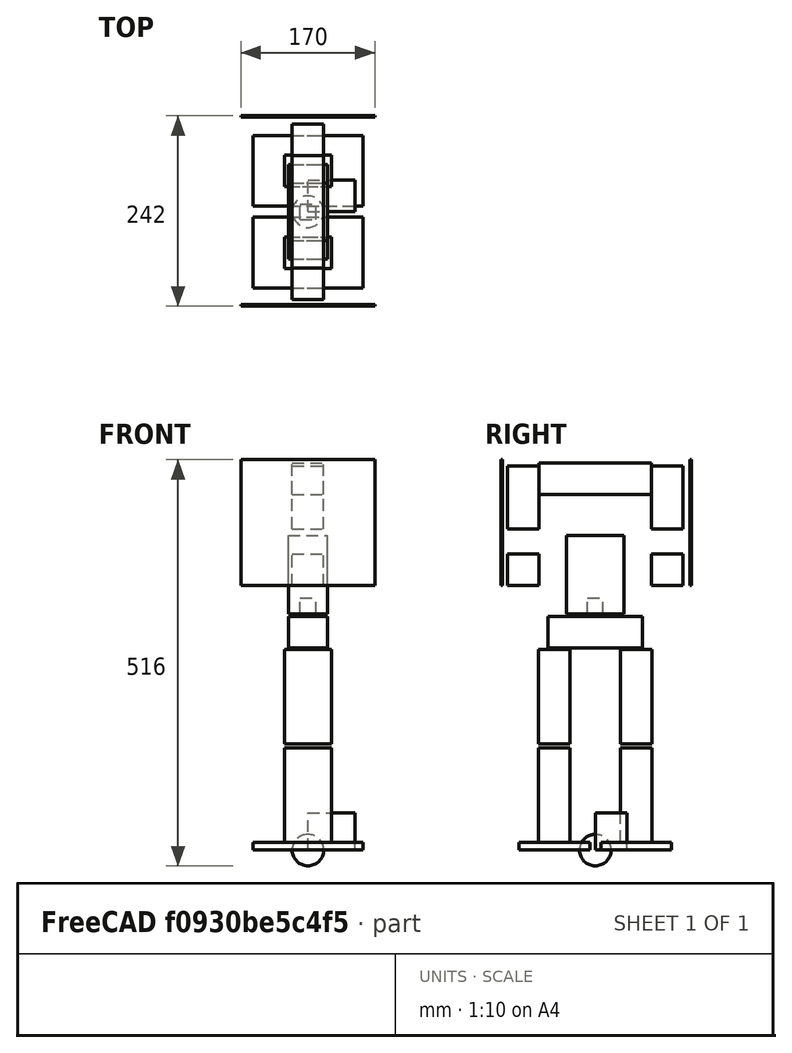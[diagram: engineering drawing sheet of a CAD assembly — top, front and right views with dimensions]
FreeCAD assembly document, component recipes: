
FREECAD ASSEMBLY — COMPONENT RECIPES ("mj_urdf")

This assembly document has 21 components, labeled P0..P20 below (a component is one placed body or linked part). 0 of them carry a construction recipe — the FreeCAD feature program that regenerates the part from scratch, quoted from this document or its linked companion documents; the rest are supplied as boundary geometry only. No exploded tour is included for this assembly.
COMPONENT P0 — geometry summary ("left_sholder001"; no construction recipe available for this part):
  bounding box: 80.0 x 40.0 x 40.0 mm
  tessellated surface: 12 triangles
  volume: 128000 mm^3 (100% of its bounding box)
  symmetry: 2-fold rotationally symmetric about the x axis; 2-fold rotationally symmetric about the y axis; 4-fold rotationally symmetric about the z axis; mirror-symmetric across its x mid-plane, z mid-plane
COMPONENT P1 — geometry summary ("real_l_body001_"; no construction recipe available for this part):
  bounding box: 161.0 x 143.0 x 50.0 mm
  tessellated surface: 36 triangles
  volume: 601800 mm^3 (52% of its bounding box)
COMPONENT P2 — geometry summary ("real_l_left_ankle001_"; no construction recipe available for this part):
  bounding box: 40.0 x 40.0 x 40.0 mm
  tessellated surface: 8,000 triangles
  volume: 33510 mm^3 (52% of its bounding box)
  symmetry: revolution-symmetric about the x axis through its bounding-box center; revolution-symmetric about the y axis through its bounding-box center; revolution-symmetric about the z axis through its bounding-box center; mirror-symmetric across its x mid-plane, y mid-plane, z mid-plane
COMPONENT P3 — geometry summary ("real_l_left_arm001_"; no construction recipe available for this part):
  bounding box: 80.0 x 40.0 x 40.0 mm
  tessellated surface: 12 triangles
  volume: 128000 mm^3 (100% of its bounding box)
  symmetry: 2-fold rotationally symmetric about the x axis; 2-fold rotationally symmetric about the y axis; 4-fold rotationally symmetric about the z axis; mirror-symmetric across its x mid-plane, z mid-plane
COMPONENT P4 — geometry summary ("real_l_left_hand001_"; no construction recipe available for this part):
  bounding box: 170.0 x 160.0 x 2.0 mm
  tessellated surface: 12 triangles
  volume: 54400 mm^3 (100% of its bounding box)
  symmetry: 2-fold rotationally symmetric about the x axis; 2-fold rotationally symmetric about the y axis; 2-fold rotationally symmetric about the z axis; mirror-symmetric across its x mid-plane, y mid-plane, z mid-plane
COMPONENT P5 — geometry summary ("real_l_left_hip001_"; no construction recipe available for this part):
  bounding box: 40.0 x 40.0 x 40.0 mm
  tessellated surface: 8,000 triangles
  volume: 33510 mm^3 (52% of its bounding box)
  symmetry: revolution-symmetric about the x axis through its bounding-box center; revolution-symmetric about the y axis through its bounding-box center; revolution-symmetric about the z axis through its bounding-box center; mirror-symmetric across its x mid-plane, y mid-plane, z mid-plane
COMPONENT P6 — geometry summary ("real_l_left_knee001_"; no construction recipe available for this part):
  bounding box: 60.0 x 47.0 x 40.0 mm
  tessellated surface: 12 triangles
  volume: 112800 mm^3 (100% of its bounding box)
  symmetry: 2-fold rotationally symmetric about the z axis; mirror-symmetric across its y mid-plane
COMPONENT P7 — geometry summary ("real_l_left_shin001_"; no construction recipe available for this part):
  bounding box: 120.0 x 60.0 x 40.0 mm
  tessellated surface: 12 triangles
  volume: 288000 mm^3 (100% of its bounding box)
  symmetry: 2-fold rotationally symmetric about the x axis; 2-fold rotationally symmetric about the y axis; mirror-symmetric across its y mid-plane
COMPONENT P8 — geometry summary ("real_l_left_sole001_"; no construction recipe available for this part):
  bounding box: 140.0 x 90.0 x 10.0 mm
  tessellated surface: 12 triangles
  volume: 126000 mm^3 (100% of its bounding box)
  symmetry: 2-fold rotationally symmetric about the y axis; 2-fold rotationally symmetric about the z axis; mirror-symmetric across its x mid-plane, y mid-plane, z mid-plane
COMPONENT P9 — geometry summary ("real_l_left_thigh001_"; no construction recipe available for this part):
  bounding box: 120.0 x 60.0 x 40.0 mm
  tessellated surface: 12 triangles
  volume: 288000 mm^3 (100% of its bounding box)
  symmetry: 2-fold rotationally symmetric about the x axis; 2-fold rotationally symmetric about the y axis; mirror-symmetric across its y mid-plane
COMPONENT P10 — geometry summary ("real_l_left_wrist001_"; no construction recipe available for this part):
  bounding box: 40.0 x 40.0 x 40.0 mm
  tessellated surface: 12 triangles
  volume: 64000 mm^3 (100% of its bounding box)
  symmetry: 4-fold rotationally symmetric about the x axis; 4-fold rotationally symmetric about the z axis; mirror-symmetric across its x mid-plane, y mid-plane, z mid-plane
COMPONENT P11 — geometry summary ("real_l_right_ankle001_"; no construction recipe available for this part):
  bounding box: 40.0 x 40.0 x 40.0 mm
  tessellated surface: 8,000 triangles
  volume: 33510 mm^3 (52% of its bounding box)
  symmetry: revolution-symmetric about the x axis through its bounding-box center; revolution-symmetric about the y axis through its bounding-box center; revolution-symmetric about the z axis through its bounding-box center; mirror-symmetric across its x mid-plane, y mid-plane, z mid-plane
COMPONENT P12 — geometry summary ("real_l_right_arm001_"; no construction recipe available for this part):
  bounding box: 80.0 x 40.0 x 40.0 mm
  tessellated surface: 12 triangles
  volume: 128000 mm^3 (100% of its bounding box)
  symmetry: 2-fold rotationally symmetric about the x axis; 2-fold rotationally symmetric about the y axis; 4-fold rotationally symmetric about the z axis; mirror-symmetric across its x mid-plane, z mid-plane
COMPONENT P13 — geometry summary ("real_l_right_hand001_"; no construction recipe available for this part):
  bounding box: 170.0 x 160.0 x 2.0 mm
  tessellated surface: 12 triangles
  volume: 54400 mm^3 (100% of its bounding box)
  symmetry: 2-fold rotationally symmetric about the x axis; 2-fold rotationally symmetric about the y axis; 2-fold rotationally symmetric about the z axis; mirror-symmetric across its x mid-plane, y mid-plane, z mid-plane
COMPONENT P14 — geometry summary ("real_l_right_hip001_"; no construction recipe available for this part):
  bounding box: 40.0 x 40.0 x 40.0 mm
  tessellated surface: 8,000 triangles
  volume: 33510 mm^3 (52% of its bounding box)
  symmetry: revolution-symmetric about the x axis through its bounding-box center; revolution-symmetric about the y axis through its bounding-box center; revolution-symmetric about the z axis through its bounding-box center; mirror-symmetric across its x mid-plane, y mid-plane, z mid-plane
COMPONENT P15 — geometry summary ("real_l_right_knee001_"; no construction recipe available for this part):
  bounding box: 60.0 x 47.0 x 40.0 mm
  tessellated surface: 12 triangles
  volume: 112800 mm^3 (100% of its bounding box)
  symmetry: 2-fold rotationally symmetric about the z axis; mirror-symmetric across its y mid-plane
COMPONENT P16 — geometry summary ("real_l_right_shin001_"; no construction recipe available for this part):
  bounding box: 120.0 x 60.0 x 40.0 mm
  tessellated surface: 12 triangles
  volume: 288000 mm^3 (100% of its bounding box)
  symmetry: 2-fold rotationally symmetric about the x axis; 2-fold rotationally symmetric about the y axis; 2-fold rotationally symmetric about the z axis; mirror-symmetric across its y mid-plane
COMPONENT P17 — geometry summary ("real_l_right_sole001_"; no construction recipe available for this part):
  bounding box: 140.0 x 90.0 x 10.0 mm
  tessellated surface: 12 triangles
  volume: 126000 mm^3 (100% of its bounding box)
  symmetry: 2-fold rotationally symmetric about the y axis; 2-fold rotationally symmetric about the z axis; mirror-symmetric across its x mid-plane, y mid-plane, z mid-plane
COMPONENT P18 — geometry summary ("real_l_right_thigh001_"; no construction recipe available for this part):
  bounding box: 120.0 x 60.0 x 40.0 mm
  tessellated surface: 12 triangles
  volume: 288000 mm^3 (100% of its bounding box)
  symmetry: 2-fold rotationally symmetric about the x axis; 2-fold rotationally symmetric about the y axis; mirror-symmetric across its y mid-plane
COMPONENT P19 — geometry summary ("real_l_right_wrist001_"; no construction recipe available for this part):
  bounding box: 40.0 x 40.0 x 40.0 mm
  tessellated surface: 12 triangles
  volume: 64000 mm^3 (100% of its bounding box)
  symmetry: 4-fold rotationally symmetric about the x axis; 4-fold rotationally symmetric about the z axis; mirror-symmetric across its x mid-plane, y mid-plane, z mid-plane
COMPONENT P20 — geometry summary ("real_l_waist001_"; no construction recipe available for this part):
  bounding box: 120.0 x 50.0 x 40.0 mm
  tessellated surface: 12 triangles
  volume: 240000 mm^3 (100% of its bounding box)
  symmetry: 2-fold rotationally symmetric about the x axis; 2-fold rotationally symmetric about the z axis; mirror-symmetric across its x mid-plane, y mid-plane, z mid-plane
PROVENANCE & LICENSES
A FreeCAD (.FCStd) document from a public repository crawl; recipes are the document's own serialized feature recipes (and, for linked parts, companion documents' recipes).
License: as declared in the source repository (recorded in the dataset sidecar).
